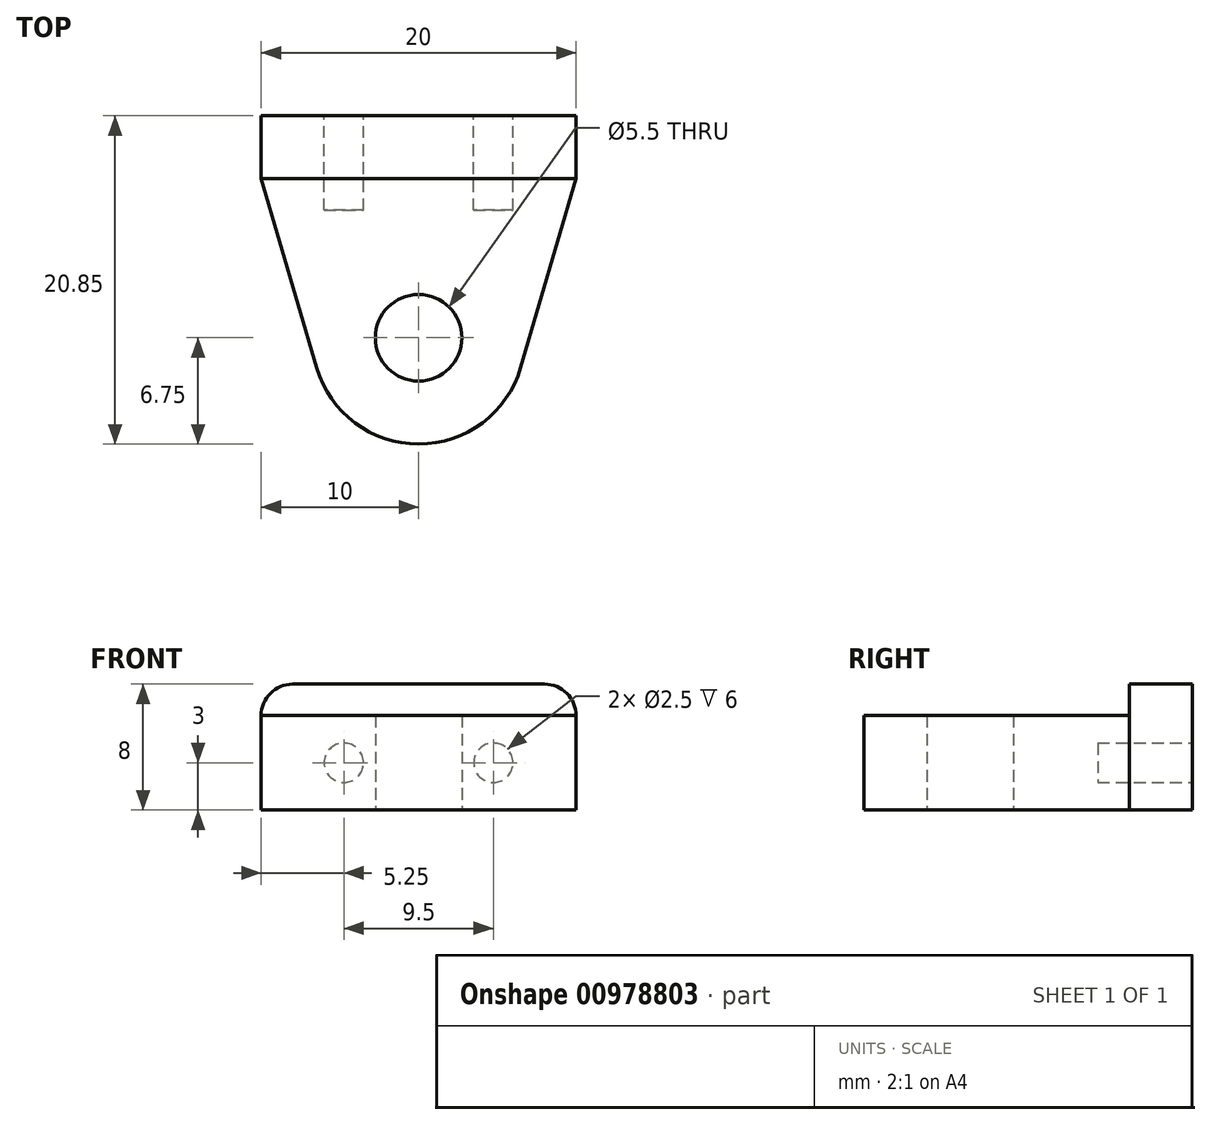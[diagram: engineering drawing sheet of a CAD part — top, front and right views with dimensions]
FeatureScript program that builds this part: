
annotation { "Feature Type Name" : "Feature", "Feature Type Description" : "" }
export const myFeature = defineFeature(function(context is Context, id is Id, definition is map)
    precondition{}
    {
        {
            var Q0;
            Q0=qCreatedBy(makeId("Top.planeOp"),FACE);
            var sketch = newSketch(context, id + "F0", { "sketchPlane" : qUnion([Q0])});
            skCircle(sketch, "E0", {"center": v(0, 0) * mm, "radius": 2.75 * mm});
            skArc(sketch, "E1", {"start": v(-6.48, -1.9) * mm, "mid": v(0, -6.75) * mm, "end": v(6.48, -1.9) * mm});
            skLineSegment(sketch, "E2.bottom", {"start": v(-10, 14.1) * mm, "end": v(10, 14.1) * mm});
            skLineSegment(sketch, "E2.top", {"start": v(-10, 10.1) * mm, "end": v(10, 10.1) * mm});
            skLineSegment(sketch, "E2.left", {"start": v(-10, 14.1) * mm, "end": v(-10, 10.1) * mm});
            skLineSegment(sketch, "E2.right", {"start": v(10, 14.1) * mm, "end": v(10, 10.1) * mm});
            skLineSegment(sketch, "E3", {"start": v(0, 10.1) * mm, "end": v(0, 0) * mm, "construction": true});
            skCircle(sketch, "E4", {"center": v(0, 0) * mm, "radius": 2.7 * mm, "construction": true});
            skLineSegment(sketch, "E5", {"start": v(-10, 10.1) * mm, "end": v(-6.48, -1.9) * mm});
            skLineSegment(sketch, "E6", {"start": v(10, 10.1) * mm, "end": v(6.48, -1.9) * mm});
            skSolve(sketch);
        }
        {
            var Q0;
            Q0=makeQuery(id+"F0.imprint","IMPRINT",FACE,{"disambiguationData":[TD([[makeQuery(id+"F0.imprint","IMPRINT",EDGE,{"derivedFrom":sQuery(id+"F0.wireOp",EDGE,"E0")}),-1.0]])]});
            extrude(context, id + "F1", {"entities" : qUnion([Q0]), "depth" : 6 * mm, "offsetDistance" : 25 * mm});
        }
        {
            var Q0;
            Q0=makeQuery(id+"F0.imprint","IMPRINT",FACE,{"disambiguationData":[TD([[makeQuery(id+"F0.imprint","IMPRINT",EDGE,{"derivedFrom":sQuery(id+"F0.wireOp",EDGE,"E2.bottom")}),-1.0]])]});
            extrude(context, id + "F2", {"entities" : qUnion([Q0]), "operationType" : NewBodyOperationType.ADD, "depth" : 8 * mm, "offsetDistance" : 25 * mm});
        }
        {
            var Q0;
            Q0=makeQuery(id+"F2.opExtrude","SWEPT_FACE",FACE,{"disambiguationData":[OSD([sQuery(id+"F0.wireOp",EDGE,"E2.bottom")])]});
            var sketch = newSketch(context, id + "F3", { "sketchPlane" : qUnion([Q0])});
            skCircle(sketch, "E7", {"center": v(-4.75, 3) * mm, "radius": 1.25 * mm});
            skCircle(sketch, "E8", {"center": v(4.75, 3) * mm, "radius": 1.25 * mm});
            skLineSegment(sketch, "E9", {"start": v(4.75, 3) * mm, "end": v(-4.75, 3) * mm, "construction": true});
            skLineSegment(sketch, "E10", {"start": v(0, 0) * mm, "end": v(0, 3) * mm, "construction": true});
            skSolve(sketch);
        }
        {
            var Q0;
            Q0=makeQuery(id+"F3.imprint","IMPRINT",FACE,{"disambiguationData":[TD([[makeQuery(id+"F3.imprint","IMPRINT",EDGE,{"derivedFrom":sQuery(id+"F3.wireOp",EDGE,"E7")}),1.0]])]});
            var Q1;
            Q1=makeQuery(id+"F3.imprint","IMPRINT",FACE,{"disambiguationData":[TD([[makeQuery(id+"F3.imprint","IMPRINT",EDGE,{"derivedFrom":sQuery(id+"F3.wireOp",EDGE,"E8")}),1.0]])]});
            extrude(context, id + "F4", {"entities" : qUnion([Q0, Q1]), "operationType" : NewBodyOperationType.REMOVE, "oppositeDirection" : true, "depth" : 6 * mm, "offsetDistance" : 25 * mm});
        }
        {
            var Q0;
            Q0=makeQuery(id+"F2.opExtrude","CAP_EDGE",EDGE,{"disambiguationData":[OSD([sQuery(id+"F0.wireOp",EDGE,"E2.left")])],"isStart":false});
            var Q1;
            Q1=makeQuery(id+"F2.opExtrude","CAP_EDGE",EDGE,{"disambiguationData":[OSD([sQuery(id+"F0.wireOp",EDGE,"E2.right")])],"isStart":false});
            fillet(context, id + "F5", {"entities" : qUnion([Q0, Q1]), "radius" : 2 * mm, "tangentPropagation" : true, "allowEdgeOverflow" : false});
        }
    });
